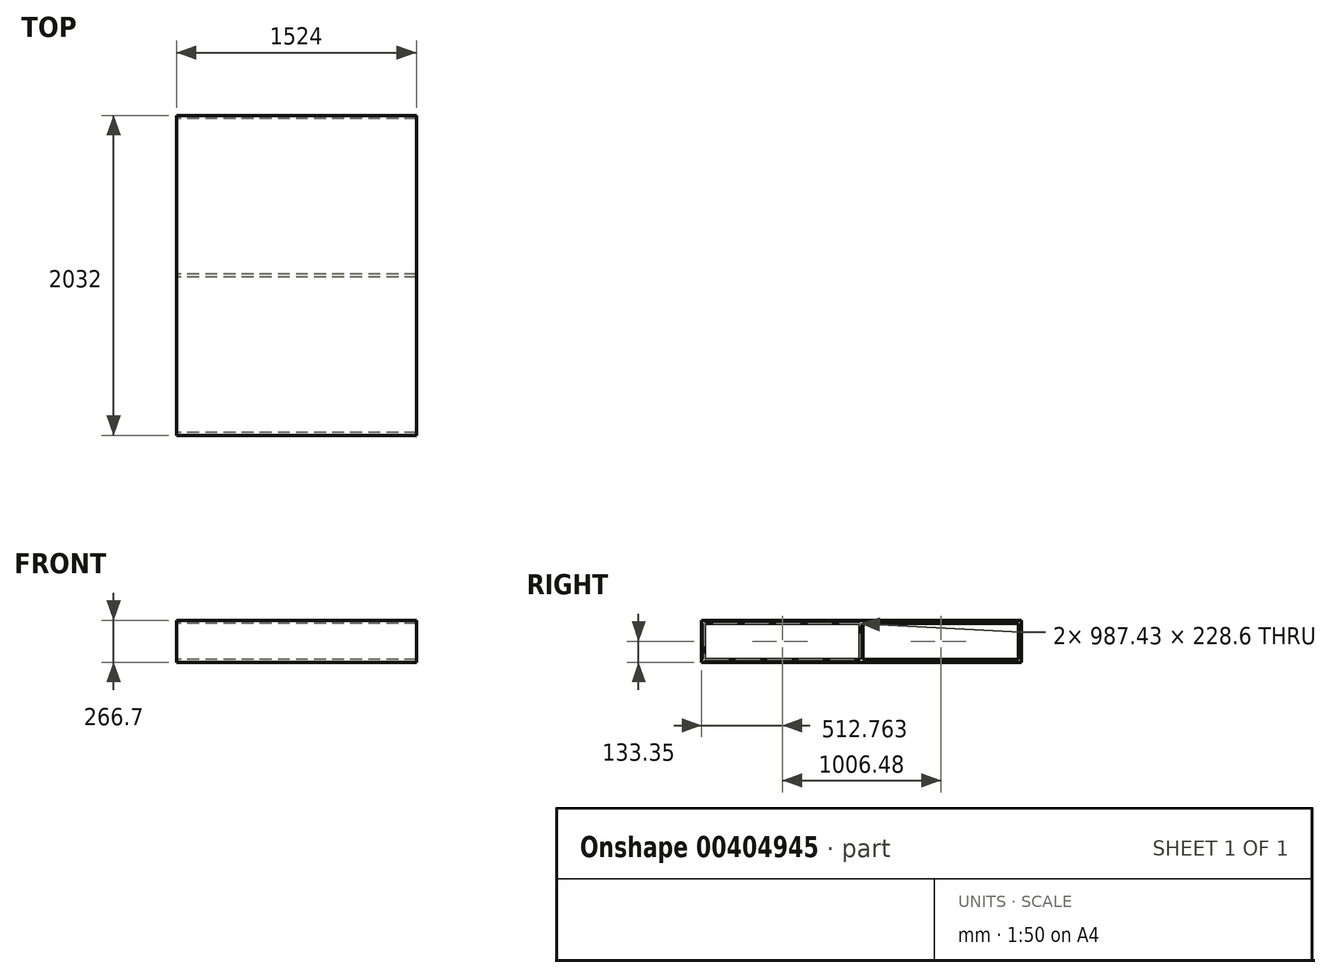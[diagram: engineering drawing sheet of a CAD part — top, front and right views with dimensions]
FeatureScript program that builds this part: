
annotation { "Feature Type Name" : "Feature", "Feature Type Description" : "" }
export const myFeature = defineFeature(function(context is Context, id is Id, definition is map)
    precondition{}
    {
        {
            var Q0;
            Q0=qCreatedBy(makeId("Right.planeOp"),FACE);
            var sketch = newSketch(context, id + "F0", { "sketchPlane" : qUnion([Q0])});
            skLineSegment(sketch, "E0.bottom", {"start": v(-1016, 266.7) * mm, "end": v(1016, 266.7) * mm});
            skLineSegment(sketch, "E0.top", {"start": v(-1016, 247.65) * mm, "end": v(1016, 247.65) * mm});
            skLineSegment(sketch, "E0.left", {"start": v(-1016, 266.7) * mm, "end": v(-1016, 247.65) * mm});
            skLineSegment(sketch, "E0.right", {"start": v(1016, 266.7) * mm, "end": v(1016, 247.65) * mm});
            skLineSegment(sketch, "E1.bottom", {"start": v(-1016, 266.7) * mm, "end": v(-996.95, 266.7) * mm});
            skLineSegment(sketch, "E1.top", {"start": v(-1016, 0) * mm, "end": v(-996.95, 0) * mm});
            skLineSegment(sketch, "E1.left", {"start": v(-1016, 266.7) * mm, "end": v(-1016, 0) * mm});
            skLineSegment(sketch, "E1.right", {"start": v(-996.95, 266.7) * mm, "end": v(-996.95, 0) * mm});
            skLineSegment(sketch, "E2.bottom", {"start": v(1016, 266.7) * mm, "end": v(996.95, 266.7) * mm});
            skLineSegment(sketch, "E2.top", {"start": v(1016, 0) * mm, "end": v(996.95, 0) * mm});
            skLineSegment(sketch, "E2.left", {"start": v(1016, 266.7) * mm, "end": v(1016, 0) * mm});
            skLineSegment(sketch, "E2.right", {"start": v(996.95, 266.7) * mm, "end": v(996.95, 0) * mm});
            skLineSegment(sketch, "E3.bottom", {"start": v(-1016, 0) * mm, "end": v(1016, 0) * mm});
            skLineSegment(sketch, "E3.top", {"start": v(-1016, 19.05) * mm, "end": v(1016, 19.05) * mm});
            skLineSegment(sketch, "E3.left", {"start": v(-1016, 0) * mm, "end": v(-1016, 19.05) * mm});
            skLineSegment(sketch, "E3.right", {"start": v(1016, 0) * mm, "end": v(1016, 19.05) * mm});
            skLineSegment(sketch, "E4", {"start": v(-1016, 19.05) * mm, "end": v(-1016, 0) * mm});
            skLineSegment(sketch, "E5", {"start": v(0, 362.4) * mm, "end": v(0, -384.63) * mm, "construction": true});
            skLineSegment(sketch, "E6.bottom", {"start": v(-9.53, 247.65) * mm, "end": v(9.52, 247.65) * mm});
            skLineSegment(sketch, "E6.top", {"start": v(-9.52, 19.05) * mm, "end": v(9.52, 19.05) * mm});
            skLineSegment(sketch, "E6.left", {"start": v(-9.53, 247.65) * mm, "end": v(-9.53, 19.05) * mm});
            skLineSegment(sketch, "E6.right", {"start": v(9.52, 247.65) * mm, "end": v(9.52, 19.05) * mm});
            skSolve(sketch);
        }
        {
            var Q0;
            {var subQ3=sQuery(id+"F0.wireOp",EDGE,"E0.left");Q0=makeQuery(id+"F0.imprint","IMPRINT",FACE,{"disambiguationData":[TD([[makeQuery(id+"F0.imprint","IMPRINT",EDGE,{"derivedFrom":subQ3}),1.0]])]});}
            var Q1;
            {var subQ0=sQuery(id+"F0.wireOp",EDGE,"E0.right");Q1=makeQuery(id+"F0.imprint","IMPRINT",FACE,{"disambiguationData":[TD([[makeQuery(id+"F0.imprint","IMPRINT",EDGE,{"derivedFrom":subQ0}),-1.0]])]});}
            var Q2;
            {var subQ0=sQuery(id+"F0.wireOp",EDGE,"E1.top");Q2=makeQuery(id+"F0.imprint","IMPRINT",FACE,{"disambiguationData":[TD([[makeQuery(id+"F0.imprint","IMPRINT",EDGE,{"derivedFrom":subQ0}),1.0]])]});}
            var Q3;
            {var subQ0=sQuery(id+"F0.wireOp",EDGE,"E2.top");Q3=makeQuery(id+"F0.imprint","IMPRINT",FACE,{"disambiguationData":[TD([[makeQuery(id+"F0.imprint","IMPRINT",EDGE,{"derivedFrom":subQ0}),-1.0]])]});}
            var Q4;
            {var subQ0=sQuery(id+"F0.wireOp",EDGE,"E1.right");var subQ1=sQuery(id+"F0.wireOp",EDGE,"E0.top");var subQ2=makeQuery(id+"F0.imprint","INTERSECT",VERTEX,{"derivedFrom":[subQ1,subQ0]});Q4=makeQuery(id+"F0.imprint","IMPRINT",FACE,{"disambiguationData":[TD([[makeQuery(id+"F0.imprint","IMPRINT",EDGE,{"disambiguationData":[TD([[subQ2,-1.0]])],"derivedFrom":subQ0}),-1.0]])]});}
            var Q5;
            {var subQ1=sQuery(id+"F0.wireOp",EDGE,"E0.top");var subQ3=sQuery(id+"F0.wireOp",EDGE,"E2.right");var subQ4=makeQuery(id+"F0.imprint","INTERSECT",VERTEX,{"derivedFrom":[subQ1,subQ3]});Q5=makeQuery(id+"F0.imprint","IMPRINT",FACE,{"disambiguationData":[TD([[makeQuery(id+"F0.imprint","IMPRINT",EDGE,{"disambiguationData":[TD([[subQ4,-1.0]])],"derivedFrom":subQ3}),1.0]])]});}
            var Q6;
            {var subQ4=sQuery(id+"F0.wireOp",EDGE,"E3.bottom");Q6=makeQuery(id+"F0.imprint","IMPRINT",FACE,{"disambiguationData":[TD([[makeQuery(id+"F0.imprint","IMPRINT",EDGE,{"derivedFrom":subQ4}),1.0]])]});}
            var Q7;
            {var subQ5=sQuery(id+"F0.wireOp",EDGE,"E1.right");var subQ7=sQuery(id+"F0.wireOp",EDGE,"E0.bottom");var subQ8=makeQuery(id+"F0.imprint","INTERSECT",VERTEX,{"derivedFrom":[subQ7,subQ5]});Q7=makeQuery(id+"F0.imprint","IMPRINT",FACE,{"disambiguationData":[TD([[makeQuery(id+"F0.imprint","IMPRINT",EDGE,{"disambiguationData":[TD([[subQ8,-1.0]])],"derivedFrom":subQ7}),-1.0]])]});}
            var Q8;
            {var subQ2=sQuery(id+"F0.wireOp",EDGE,"E6.left");Q8=makeQuery(id+"F0.imprint","IMPRINT",FACE,{"disambiguationData":[TD([[makeQuery(id+"F0.imprint","IMPRINT",EDGE,{"derivedFrom":subQ2}),1.0]])]});}
            extrude(context, id + "F1", {"entities" : qUnion([Q0, Q1, Q2, Q3, Q4, Q5, Q6, Q7, Q8]), "depth" : 1524 * mm});
        }
    });
